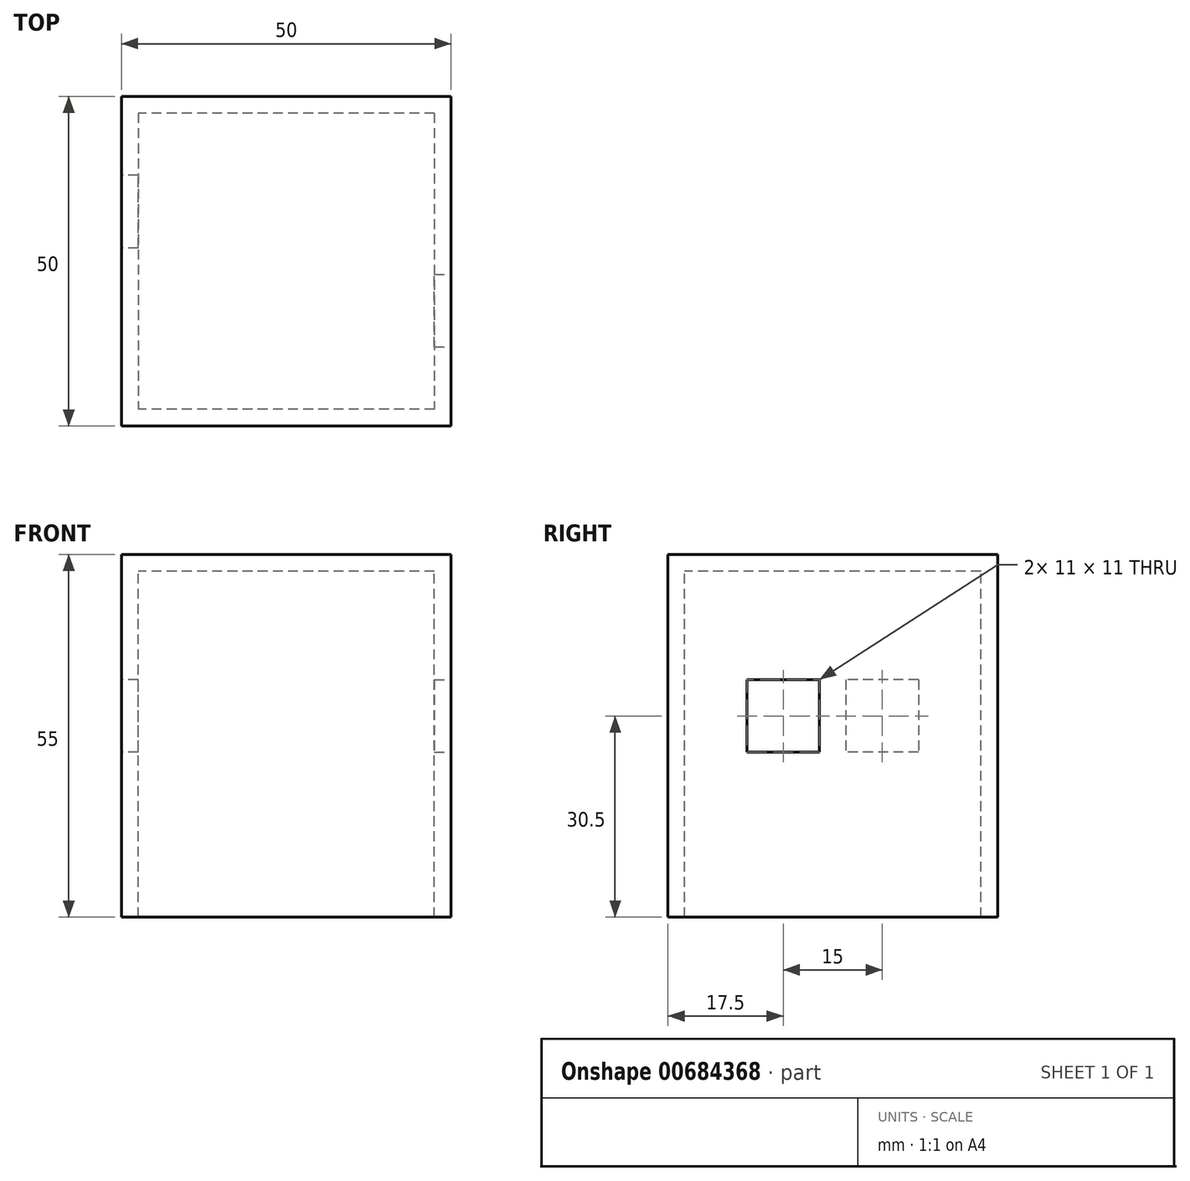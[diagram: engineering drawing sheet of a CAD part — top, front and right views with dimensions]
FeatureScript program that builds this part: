
annotation { "Feature Type Name" : "Feature", "Feature Type Description" : "" }
export const myFeature = defineFeature(function(context is Context, id is Id, definition is map)
    precondition{}
    {
        {
            var Q0;
            Q0=qCreatedBy(makeId("Front.planeOp"),FACE);
            var sketch = newSketch(context, id + "F0", { "sketchPlane" : qUnion([Q0])});
            skLineSegment(sketch, "E0.bottom", {"start": v(25, -27.5) * mm, "end": v(-25, -27.5) * mm});
            skLineSegment(sketch, "E0.top", {"start": v(25, 27.5) * mm, "end": v(-25, 27.5) * mm});
            skLineSegment(sketch, "E0.left", {"start": v(25, -27.5) * mm, "end": v(25, 27.5) * mm});
            skLineSegment(sketch, "E0.right", {"start": v(-25, -27.5) * mm, "end": v(-25, 27.5) * mm});
            skPoint(sketch, "E0.middle", {"position": v(0, 0) * mm});
            skSolve(sketch);
        }
        {
            var Q0;
            Q0=makeQuery(id+"F0.imprint","IMPRINT",FACE,{"disambiguationData":[TD([[makeQuery(id+"F0.imprint","IMPRINT",EDGE,{"derivedFrom":sQuery(id+"F0.wireOp",EDGE,"E0.bottom")}),-1.0]])]});
            extrude(context, id + "F1", {"entities" : qUnion([Q0]), "oppositeDirection" : true, "depth" : 50 * mm, "offsetDistance" : 25.4 * mm});
        }
        {
            var Q0;
            Q0=makeQuery(id+"F1.opExtrude","SWEPT_FACE",FACE,{"disambiguationData":[OSD([sQuery(id+"F0.wireOp",EDGE,"E0.bottom")])]});
            var Q1;
            Q1=makeQuery(id+"F1.opExtrude","SWEPT_BODY",BODY,{"disambiguationData":[OSD([sQuery(id+"F0.wireOp",EDGE,"E0.bottom"),sQuery(id+"F0.wireOp",EDGE,"E0.top"),sQuery(id+"F0.wireOp",EDGE,"E0.left"),sQuery(id+"F0.wireOp",EDGE,"E0.right")])]});
            shell(context, id + "F2", {"entities" : qUnion([Q0]), "parts" : qUnion([Q1]), "thickness" : 2.54 * mm});
        }
        {
            var Q0;
            Q0=makeQuery(id+"F1.opExtrude","SWEPT_FACE",FACE,{"disambiguationData":[OSD([sQuery(id+"F0.wireOp",EDGE,"E0.right")])]});
            var sketch = newSketch(context, id + "F3", { "sketchPlane" : qUnion([Q0])});
            skLineSegment(sketch, "E1.bottom", {"start": v(-38, 8.5) * mm, "end": v(-27, 8.5) * mm});
            skLineSegment(sketch, "E1.top", {"start": v(-38, -2.5) * mm, "end": v(-27, -2.5) * mm});
            skLineSegment(sketch, "E1.left", {"start": v(-38, 8.5) * mm, "end": v(-38, -2.5) * mm});
            skLineSegment(sketch, "E1.right", {"start": v(-27, 8.5) * mm, "end": v(-27, -2.5) * mm});
            skSolve(sketch);
        }
        {
            var Q0;
            Q0 = qSketchRegion(id + "F3", true);
            extrude(context, id + "F4", {"entities" : qUnion([Q0]), "operationType" : NewBodyOperationType.REMOVE, "oppositeDirection" : true, "depth" : 10 * mm, "offsetDistance" : 25.4 * mm});
        }
        {
            var Q0;
            Q0=makeQuery(id+"F1.opExtrude","SWEPT_FACE",FACE,{"disambiguationData":[OSD([sQuery(id+"F0.wireOp",EDGE,"E0.left")])]});
            var sketch = newSketch(context, id + "F5", { "sketchPlane" : qUnion([Q0])});
            skLineSegment(sketch, "E2.bottom", {"start": v(12, 8.5) * mm, "end": v(23, 8.5) * mm});
            skLineSegment(sketch, "E2.top", {"start": v(12, -2.5) * mm, "end": v(23, -2.5) * mm});
            skLineSegment(sketch, "E2.left", {"start": v(12, 8.5) * mm, "end": v(12, -2.5) * mm});
            skLineSegment(sketch, "E2.right", {"start": v(23, 8.5) * mm, "end": v(23, -2.5) * mm});
            skSolve(sketch);
        }
        {
            var Q0;
            Q0=makeQuery(id+"F5.imprint","IMPRINT",FACE,{"disambiguationData":[TD([[makeQuery(id+"F5.imprint","IMPRINT",EDGE,{"derivedFrom":sQuery(id+"F5.wireOp",EDGE,"E2.bottom")}),-1.0]])]});
            extrude(context, id + "F6", {"entities" : qUnion([Q0]), "operationType" : NewBodyOperationType.REMOVE, "oppositeDirection" : true, "depth" : 10 * mm, "offsetDistance" : 25.4 * mm});
        }
    });
